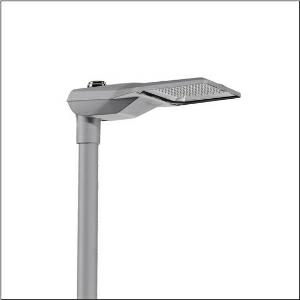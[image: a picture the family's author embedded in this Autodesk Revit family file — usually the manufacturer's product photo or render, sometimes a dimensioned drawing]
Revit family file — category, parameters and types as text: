
# Revit family: streetlight_sl_21_midi___stw1_0a_5xe7e37n08lb_0f97
name_source: partatom
category: Lighting Fixtures
units: mm (PartAtom-declared; Revit-internal decimal feet)

## family parameters
Cut with Voids When Loaded = No
Host = Face
Light Source = No
Part Type = Normal
Room Calculation Point = No
Round Connector Dimension = Use Diameter
Shared = No

## types (1)
- --- (1 x LED, 14340 lm, 98.3 W, 3000K)
    Apparent Load = 98 VA
    CIE Flux Codes = 38 75 98 100 100
    Color Rendering = 70
    Color Temperature = 3000K
    Default Elevation = 1800 mm
    Description = Streetlight SL 21 midi, mast luminaire, primary light control with lens, of PMMA, primary optical cover: cover, of toughened safety glass, transparent, light distribution: STW1.0a, light emission: direct distribution, primary light characteristic: asymmetric, installation type: side-entry, LED, 3G 2.5mm², High Power LED, rated luminous flux: 14.340lm, luminous efficacy: 146lm/W, light colour: 730, colour temperature: 3000K, control gear: NEMA (7pin), control: overheat protection, pre-setting: linear dimming characteristic, constant luminous flux control, time-dependent luminous flux control, flexible luminous flux parameterisation, mains connection: 220..240V, AC, 50/60Hz, connection cable pre-assembled, cable length: 10,5m, wiring characteristics: H05VV-F, start of lifetime: 98W, end of service life: 101W, reduction: 45W, luminaire housing, of diecast aluminium (EN AC-44300), powder-coated, Siteco® metallic grey (DB 702S), corrosivity category C5 mid according to DIN EN ISO 12944, multi-level sealing system, sealing non-destructively replaceable, inclination adjustable: 0°, 5°, 10°, 15°, length: 644mm, width: 335mm, height: 110mm, spigot size: 42mm (side-entry), mounting height: 4..8m, protection rating (complete): IP66, insulation class (complete): insulation class I (protective earthing), certification: CE, ENEC, ENEC+, VDE, impact resistance: IK10, permissible operating ambient temperature for outdoor applications: -40..+50°C, standard-compliant lighting for roads and squares, packaging unit: 1 piece

Light Distribution: STW1.0a
    Height = 111 mm
    Lamp = 1 x LED
    Lamp Light Flux = 14340 lm
    Lamp Power = 98.3 W
    Lamp count = 1
    Length = 644 mm
    Luminous efficacy = 146 lm/W
    Manufacturer = Siteco
    ModVariant = No
    Model = 5XE7E37N08LB
    Number of Poles = 1
    OnlyDefault = Yes
    Power Factor = 1
    Product Name = Streetlight SL 21 midi | STW1.0a
    Product group = mast luminaire | pylon top
    ProductGroupID = 6100
    Protection Class = Protection class I
    Protection Degree = IP 66
    RLX_Detail_Level = 1
    RLX_Emergency_Light_Flux = 0 lm
    RLX_Emergency_Type = 0
    RLX_Emergency_Type_DB = No
    RlxData = <blob elided: 26701 chars, md5=baa16b10>
    Socket = socket
    Standby Power = 0 W
    System Light Flux = 14340 lm
    System Power = 98 W
    Type Comments = factory setting: luminous flux: 100 % | dim-lin: 254 | 1020 mA
    Type Image = l_1294377.jpg
    URL = http://relux.com
    VarID = @adj_157037
    Voltage = 0 V
    Weight = 0.00 kg
    Width = 336 mm

## geometry (parser evidence)
native form markers: Blend x4, Sweep x10
no freeform markers — native parametric forms only
